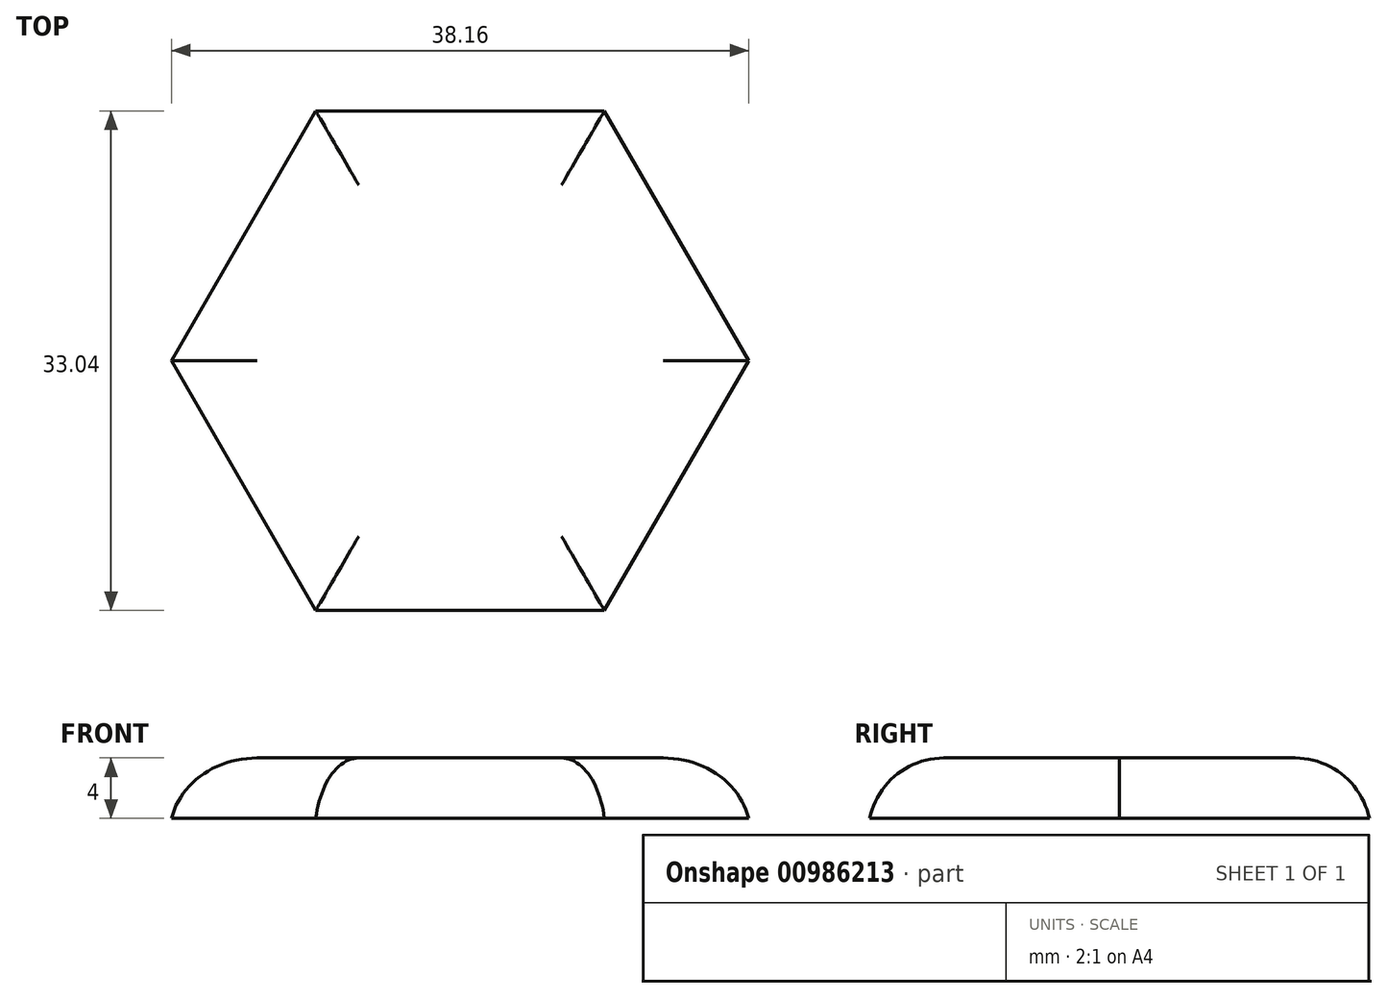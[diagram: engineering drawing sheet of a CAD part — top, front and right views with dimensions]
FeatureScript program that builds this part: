
annotation { "Feature Type Name" : "Feature", "Feature Type Description" : "" }
export const myFeature = defineFeature(function(context is Context, id is Id, definition is map)
    precondition{}
    {
        {
            var Q0;
            Q0=qCreatedBy(makeId("Top.planeOp"),FACE);
            var sketch = newSketch(context, id + "F0", { "sketchPlane" : qUnion([Q0])});
            skLineSegment(sketch, "E0", {"start": v(0, 0) * mm, "end": v(19.08, 0) * mm});
            skLineSegment(sketch, "E1", {"start": v(0, 0) * mm, "end": v(9.54, -16.52) * mm});
            skLineSegment(sketch, "E2", {"start": v(0, 0) * mm, "end": v(-9.54, -16.52) * mm});
            skLineSegment(sketch, "E3", {"start": v(0, 0) * mm, "end": v(-19.08, 0) * mm});
            skLineSegment(sketch, "E4", {"start": v(0, 0) * mm, "end": v(-9.54, 16.52) * mm});
            skLineSegment(sketch, "E5", {"start": v(0, 0) * mm, "end": v(9.54, 16.52) * mm});
            skLineSegment(sketch, "E6", {"start": v(9.54, 16.52) * mm, "end": v(-9.54, 16.52) * mm});
            skLineSegment(sketch, "E7", {"start": v(-9.54, 16.52) * mm, "end": v(-19.08, 0) * mm});
            skLineSegment(sketch, "E8", {"start": v(-19.08, 0) * mm, "end": v(-9.54, -16.52) * mm});
            skLineSegment(sketch, "E9", {"start": v(-9.54, -16.52) * mm, "end": v(9.54, -16.52) * mm});
            skLineSegment(sketch, "E10", {"start": v(9.54, -16.52) * mm, "end": v(19.08, 0) * mm});
            skLineSegment(sketch, "E11", {"start": v(19.08, 0) * mm, "end": v(9.54, 16.52) * mm});
            skSolve(sketch);
        }
        {
            var Q0;
            Q0=makeQuery(id+"F0.imprint","IMPRINT",FACE,{"disambiguationData":[TD([[makeQuery(id+"F0.imprint","IMPRINT",EDGE,{"derivedFrom":sQuery(id+"F0.wireOp",EDGE,"E4")}),-1.0]])]});
            var Q1;
            Q1=makeQuery(id+"F0.imprint","IMPRINT",FACE,{"disambiguationData":[TD([[makeQuery(id+"F0.imprint","IMPRINT",EDGE,{"derivedFrom":sQuery(id+"F0.wireOp",EDGE,"E3")}),-1.0]])]});
            var Q2;
            Q2=makeQuery(id+"F0.imprint","IMPRINT",FACE,{"disambiguationData":[TD([[makeQuery(id+"F0.imprint","IMPRINT",EDGE,{"derivedFrom":sQuery(id+"F0.wireOp",EDGE,"E2")}),-1.0]])]});
            var Q3;
            Q3=makeQuery(id+"F0.imprint","IMPRINT",FACE,{"disambiguationData":[TD([[makeQuery(id+"F0.imprint","IMPRINT",EDGE,{"derivedFrom":sQuery(id+"F0.wireOp",EDGE,"E1")}),-1.0]])]});
            var Q4;
            Q4=makeQuery(id+"F0.imprint","IMPRINT",FACE,{"disambiguationData":[TD([[makeQuery(id+"F0.imprint","IMPRINT",EDGE,{"derivedFrom":sQuery(id+"F0.wireOp",EDGE,"E0")}),-1.0]])]});
            var Q5;
            Q5=makeQuery(id+"F0.imprint","IMPRINT",FACE,{"disambiguationData":[TD([[makeQuery(id+"F0.imprint","IMPRINT",EDGE,{"derivedFrom":sQuery(id+"F0.wireOp",EDGE,"E0")}),1.0]])]});
            extrude(context, id + "F1", {"entities" : qUnion([Q0, Q1, Q2, Q3, Q4, Q5]), "depth" : 4 * mm, "offsetDistance" : 25 * mm});
        }
        {
            var Q0;
            Q0=makeQuery(id+"F1.opExtrude","CAP_EDGE",EDGE,{"disambiguationData":[OSD([sQuery(id+"F0.wireOp",EDGE,"E6")])],"isStart":false});
            var Q1;
            Q1=makeQuery(id+"F1.opExtrude","CAP_EDGE",EDGE,{"disambiguationData":[OSD([sQuery(id+"F0.wireOp",EDGE,"E7")])],"isStart":false});
            var Q2;
            Q2=makeQuery(id+"F1.opExtrude","CAP_EDGE",EDGE,{"disambiguationData":[OSD([sQuery(id+"F0.wireOp",EDGE,"E8")])],"isStart":false});
            var Q3;
            Q3=makeQuery(id+"F1.opExtrude","CAP_EDGE",EDGE,{"disambiguationData":[OSD([sQuery(id+"F0.wireOp",EDGE,"E11")])],"isStart":false});
            var Q4;
            Q4=makeQuery(id+"F1.opExtrude","CAP_EDGE",EDGE,{"disambiguationData":[OSD([sQuery(id+"F0.wireOp",EDGE,"E9")])],"isStart":false});
            var Q5;
            Q5=makeQuery(id+"F1.opExtrude","CAP_EDGE",EDGE,{"disambiguationData":[OSD([sQuery(id+"F0.wireOp",EDGE,"E10")])],"isStart":false});
            fillet(context, id + "F2", {"entities" : qUnion([Q0, Q1, Q2, Q3, Q4, Q5]), "radius" : 5 * mm, "tangentPropagation" : true, "allowEdgeOverflow" : false});
        }
    });
